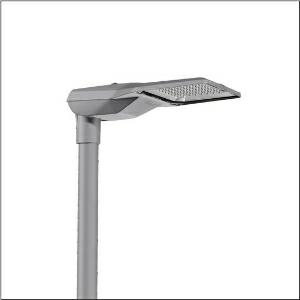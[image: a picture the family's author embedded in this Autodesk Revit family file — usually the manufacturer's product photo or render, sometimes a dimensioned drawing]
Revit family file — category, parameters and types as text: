
# Revit family: streetlight_sl_21_midi___pc-r_5xe3g43s08mb_dfdb
name_source: partatom
category: Lighting Fixtures
units: mm (PartAtom-declared; Revit-internal decimal feet)

## family parameters
Cut with Voids When Loaded = No
Host = Face
Light Source = No
Part Type = Normal
Room Calculation Point = No
Round Connector Dimension = Use Diameter
Shared = No

## types (1)
- --- (1 x LED, 19200 lm, 147 W, 4000K)
    Apparent Load = 147 VA
    CIE Flux Codes = 38 78 98 100 100
    Color Rendering = 70
    Color Temperature = 4000K
    Default Elevation = 1800 mm
    Description = Streetlight SL 21 midi, mast luminaire, primary light control with lens, of PMMA, primary optical cover: cover, of toughened safety glass, transparent, light distribution: PC-R, light emission: direct distribution, primary light characteristic: asymmetric, right, installation type: side-entry, post-top, LED, High Power LED, rated luminous flux: 19.200lm, luminous efficacy: 131lm/W, light colour: 740, colour temperature: 4000K, control gear: D4i, control: overheat protection, constant luminous flux control, time-dependent luminous flux control, flexible luminous flux parameterisation, pre-setting: logarithmic dimming characteristic, mains connection: 230..240V, AC, 50/60Hz, start of lifetime: 147W, end of service life: 155W, reduction: 65W, luminaire housing, of diecast aluminium, powder-coated, SITECO metallic grey (DB 702S), corrosivity category C5 high according to DIN EN ISO 12944, please order mast flange separately, inclination adjustable: 0°, 5°, 10°, 15°, sealing non-destructively replaceable, multi-level sealing system, length: 644mm, width: 335mm, height: 110mm, mast flange for spigot size: 42mm (side-entry): 5XC10008XM4, 60/48mm (side-entry/post-top): 5XC10108XM2, 76/60mm (side-entry/post-top): 5XC10108XM1, mounting height: 4..8m, Smart Interface above, protection rating (complete): IP66, insulation class (complete): insulation class II (safety insulation), certification: CE, ENEC, ENEC+, VDE, impact resistance: IK10, permissible operating ambient temperature for outdoor applications: -40..+50°C, standard-compliant lighting for roads and squares, packaging unit: 1 piece

Light Distribution: PC-R
    Height = 111 mm
    Lamp = 1 x LED
    Lamp Light Flux = 19200 lm
    Lamp Power = 147 W
    Lamp count = 1
    Length = 644 mm
    Luminous efficacy = 131 lm/W
    Manufacturer = Siteco
    ModVariant = No
    Model = 5XE3G43S08MB
    Number of Poles = 1
    OnlyDefault = Yes
    Power Factor = 1
    Product Name = Streetlight SL 21 midi | PC-R
    Product group = mast luminaire | pylon top
    ProductGroupID = 6100
    Protection Class = Protection class II
    Protection Degree = IP 66
    RLX_Detail_Level = 1
    RLX_Emergency_Light_Flux = 0 lm
    RLX_Emergency_Type = 0
    RLX_Emergency_Type_DB = No
    RlxData = <blob elided: 29401 chars, md5=22b9132c>
    Socket = socket
    Standby Power = 0 W
    System Light Flux = 19200 lm
    System Power = 147 W
    Type Comments = factory setting: luminous flux: 100 % | dim-lin: 254 | 750 mA
    Type Image = l_1004302.jpg
    URL = http://relux.com
    VarID = @adj_071661
    Voltage = 0 V
    Weight = 0.00 kg
    Width = 336 mm

## geometry (parser evidence)
native form markers: Blend x4, Sweep x11
no freeform markers — native parametric forms only
